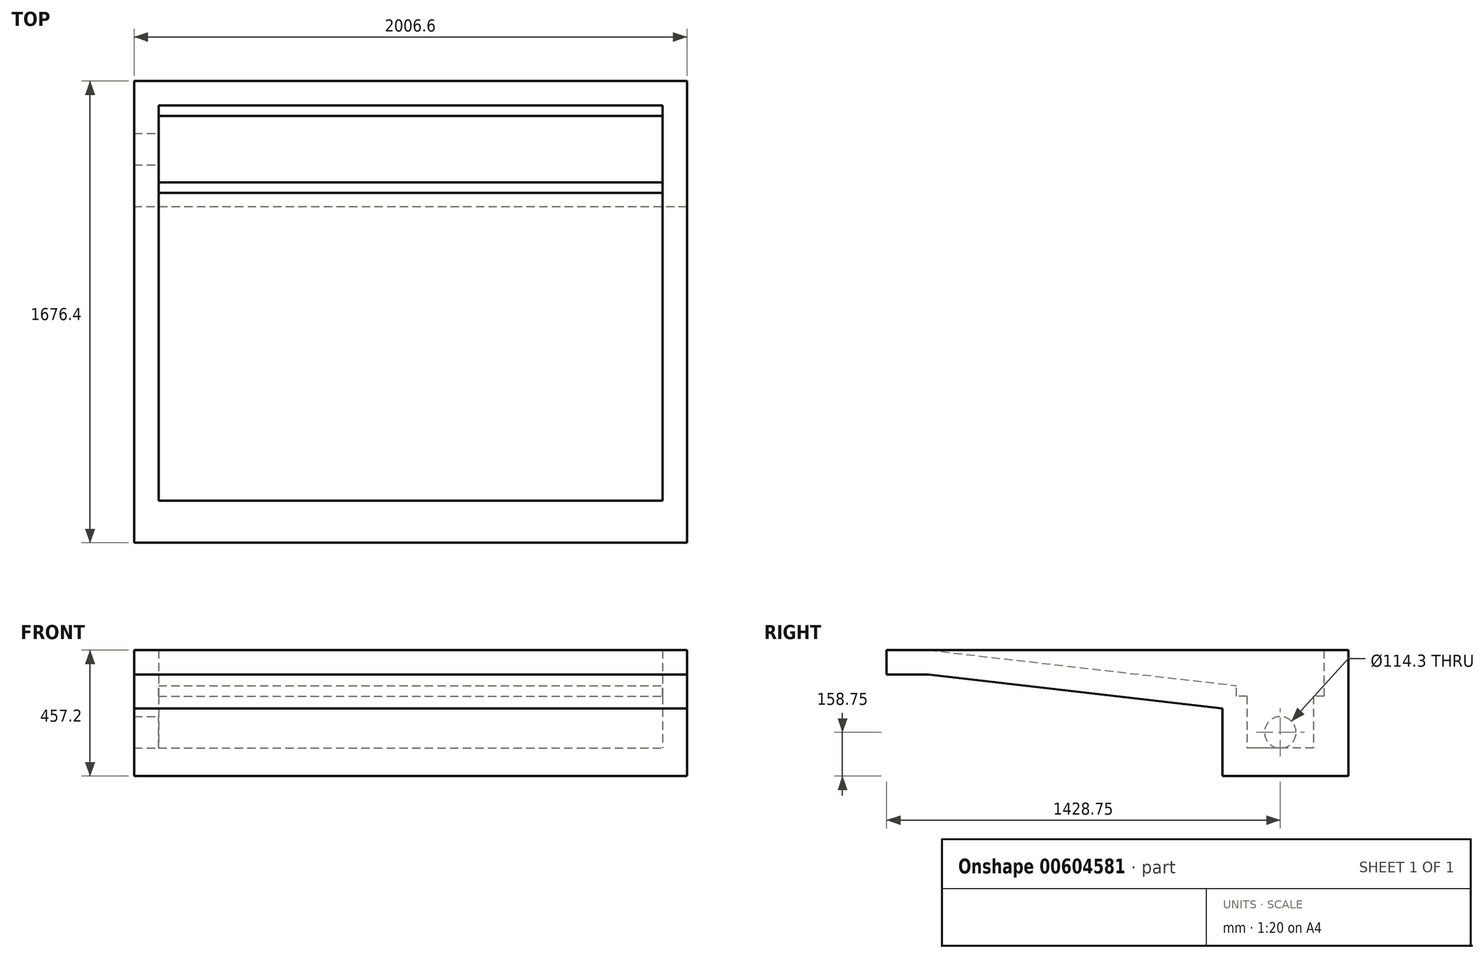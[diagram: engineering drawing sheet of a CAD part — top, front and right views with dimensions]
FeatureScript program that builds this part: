
annotation { "Feature Type Name" : "Feature", "Feature Type Description" : "" }
export const myFeature = defineFeature(function(context is Context, id is Id, definition is map)
    precondition{}
    {
        {
            var Q0;
            Q0=qCreatedBy(makeId("Top.planeOp"),FACE);
            var sketch = newSketch(context, id + "F0", { "sketchPlane" : qUnion([Q0])});
            skLineSegment(sketch, "E0.bottom", {"start": v(1003.3, 762) * mm, "end": v(-1003.3, 762) * mm});
            skLineSegment(sketch, "E0.top", {"start": v(1003.3, -762) * mm, "end": v(-1003.3, -762) * mm});
            skLineSegment(sketch, "E0.left", {"start": v(1003.3, 762) * mm, "end": v(1003.3, -762) * mm});
            skLineSegment(sketch, "E0.right", {"start": v(-1003.3, 762) * mm, "end": v(-1003.3, -762) * mm});
            skPoint(sketch, "E0.middle", {"position": v(0, 0) * mm});
            skSolve(sketch);
        }
        {
            var Q0;
            Q0=qSketchRegion(id+"F0",true);
            extrude(context, id + "F1", {"entities" : qUnion([Q0]), "depth" : 254 * mm, "offsetDistance" : 25.4 * mm});
        }
        {
            var Q0;
            Q0=qCreatedBy(makeId("Right.planeOp"),FACE);
            var sketch = newSketch(context, id + "F2", { "sketchPlane" : qUnion([Q0])});
            skLineSegment(sketch, "E1", {"start": v(-762, 254) * mm, "end": v(673.1, 88.9) * mm});
            skLineSegment(sketch, "E2", {"start": v(673.1, 88.9) * mm, "end": v(673.1, 254) * mm});
            skLineSegment(sketch, "E3", {"start": v(673.1, 254) * mm, "end": v(-762, 254) * mm});
            skLineSegment(sketch, "E4", {"start": v(-762, 165.1) * mm, "end": v(673.1, 0) * mm});
            skLineSegment(sketch, "E5", {"start": v(673.1, 0) * mm, "end": v(-762, 0) * mm});
            skLineSegment(sketch, "E6", {"start": v(-762, 0) * mm, "end": v(-762, 165.1) * mm});
            skSolve(sketch);
        }
        {
            var Q0;
            Q0=makeQuery(id+"F1.opExtrude","SWEPT_FACE",FACE,{"disambiguationData":[OSD([sQuery(id+"F0.wireOp",EDGE,"E0.right")])]});
            var sketch = newSketch(context, id + "F3", { "sketchPlane" : qUnion([Q0])});
            skLineSegment(sketch, "E7.bottom", {"start": v(-762, 254) * mm, "end": v(-304.8, 254) * mm});
            skLineSegment(sketch, "E7.top", {"start": v(-762, -203.2) * mm, "end": v(-304.8, -203.2) * mm});
            skLineSegment(sketch, "E7.left", {"start": v(-762, 254) * mm, "end": v(-762, -203.2) * mm});
            skLineSegment(sketch, "E7.right", {"start": v(-304.8, 254) * mm, "end": v(-304.8, -203.2) * mm});
            skSolve(sketch);
        }
        {
            var Q0;
            Q0=qSketchRegion(id+"F2",true);
            extrude(context, id + "F4", {"entities" : qUnion([Q0]), "operationType" : NewBodyOperationType.REMOVE, "endBound" : BoundingType.SYMMETRIC, "depth" : 1828.8 * mm, "offsetDistance" : 25.4 * mm});
        }
        {
            var Q0;
            Q0=makeQuery(id+"F4.boolean.opBoolean","COPY",FACE,{"derivedFrom":makeQuery(id+"F4.opExtrude","CAP_FACE",FACE,{"disambiguationData":[OSD([sQuery(id+"F2.wireOp",EDGE,"E4"),sQuery(id+"F2.wireOp",EDGE,"E5"),sQuery(id+"F2.wireOp",EDGE,"E6")])],"isStart":true})});
            extrude(context, id + "F5", {"entities" : qUnion([Q0]), "operationType" : NewBodyOperationType.REMOVE, "endBound" : BoundingType.THROUGH_ALL, "oppositeDirection" : true, "depth" : 25.4 * mm, "offsetDistance" : 25.4 * mm});
        }
        {
            var Q0;
            Q0=makeQuery(id+"F4.boolean.opBoolean","COPY",FACE,{"derivedFrom":makeQuery(id+"F4.opExtrude","CAP_FACE",FACE,{"disambiguationData":[OSD([sQuery(id+"F2.wireOp",EDGE,"E4"),sQuery(id+"F2.wireOp",EDGE,"E5"),sQuery(id+"F2.wireOp",EDGE,"E6")])],"isStart":false})});
            extrude(context, id + "F6", {"entities" : qUnion([Q0]), "operationType" : NewBodyOperationType.REMOVE, "endBound" : BoundingType.THROUGH_ALL, "oppositeDirection" : true, "depth" : 25.4 * mm, "offsetDistance" : 25.4 * mm});
        }
        {
            var Q0;
            Q0=qSketchRegion(id+"F3",true);
            var Q1;
            Q1=makeQuery(id+"F1.opExtrude","SWEPT_FACE",FACE,{"disambiguationData":[OSD([sQuery(id+"F0.wireOp",EDGE,"E0.left")])]});
            extrude(context, id + "F7", {"entities" : qUnion([Q0]), "operationType" : NewBodyOperationType.ADD, "endBound" : BoundingType.UP_TO_SURFACE, "oppositeDirection" : true, "depth" : 25.4 * mm, "endBoundEntityFace" : qUnion([Q1]), "offsetDistance" : 25.4 * mm});
        }
        {
            var Q0;
            Q0=makeQuery(id+"F2.imprint","IMPRINT",FACE,{"disambiguationData":[TD([[makeQuery(id+"F2.imprint","IMPRINT",EDGE,{"derivedFrom":sQuery(id+"F2.wireOp",EDGE,"E1")}),1.0]])]});
            var Q1;
            Q1=makeQuery(id+"F4.boolean.opBoolean","COPY",FACE,{"derivedFrom":makeQuery(id+"F4.opExtrude","CAP_FACE",FACE,{"disambiguationData":[OSD([sQuery(id+"F2.wireOp",EDGE,"E1"),sQuery(id+"F2.wireOp",EDGE,"E2"),sQuery(id+"F2.wireOp",EDGE,"E3")])],"isStart":true})});
            var Q2;
            Q2=makeQuery(id+"F4.boolean.opBoolean","COPY",FACE,{"derivedFrom":makeQuery(id+"F4.opExtrude","CAP_FACE",FACE,{"disambiguationData":[OSD([sQuery(id+"F2.wireOp",EDGE,"E1"),sQuery(id+"F2.wireOp",EDGE,"E2"),sQuery(id+"F2.wireOp",EDGE,"E3")])],"isStart":false})});
            extrude(context, id + "F8", {"entities" : qUnion([Q0]), "operationType" : NewBodyOperationType.REMOVE, "endBound" : BoundingType.UP_TO_SURFACE, "oppositeDirection" : true, "depth" : 25.4 * mm, "endBoundEntityFace" : qUnion([Q1]), "offsetDistance" : 25.4 * mm, "hasSecondDirection" : true, "secondDirectionBound" : SecondDirectionBoundingType.UP_TO_SURFACE, "secondDirectionOppositeDirection" : false, "secondDirectionDepth" : 25.4 * mm, "secondDirectionBoundEntityFace" : qUnion([Q2])});
        }
        {
            var Q0;
            Q0=makeQuery(id+"F7.boolean.opBoolean","MERGE",FACE,{"derivedFrom":[makeQuery(id+"F1.opExtrude","CAP_FACE",FACE,{"disambiguationData":[OSD([sQuery(id+"F0.wireOp",EDGE,"E0.bottom"),sQuery(id+"F0.wireOp",EDGE,"E0.top"),sQuery(id+"F0.wireOp",EDGE,"E0.left"),sQuery(id+"F0.wireOp",EDGE,"E0.right")])],"isStart":false}),makeQuery(id+"F7.opExtrude","SWEPT_FACE",FACE,{"disambiguationData":[OSD([sQuery(id+"F3.wireOp",EDGE,"E7.bottom")])]})]});
            var sketch = newSketch(context, id + "F9", { "sketchPlane" : qUnion([Q0])});
            skLineSegment(sketch, "E8.bottom", {"start": v(-914.4, 673.1) * mm, "end": v(914.4, 673.1) * mm});
            skLineSegment(sketch, "E8.top", {"start": v(-914.4, 355.6) * mm, "end": v(914.4, 355.6) * mm});
            skLineSegment(sketch, "E8.left", {"start": v(-914.4, 673.1) * mm, "end": v(-914.4, 355.6) * mm});
            skLineSegment(sketch, "E8.right", {"start": v(914.4, 673.1) * mm, "end": v(914.4, 355.6) * mm});
            skSolve(sketch);
        }
        {
            var Q0;
            Q0=qSketchRegion(id+"F9",true);
            var Q1;
            Q1=makeQuery(id+"F7.opExtrude","SWEPT_FACE",FACE,{"disambiguationData":[OSD([sQuery(id+"F3.wireOp",EDGE,"E7.top")])]});
            extrude(context, id + "F10", {"entities" : qUnion([Q0]), "operationType" : NewBodyOperationType.REMOVE, "endBound" : BoundingType.UP_TO_SURFACE, "oppositeDirection" : true, "depth" : 25.4 * mm, "endBoundEntityFace" : qUnion([Q1]), "hasOffset" : true, "offsetDistance" : 101.6 * mm});
        }
        {
            var Q0;
            Q0=makeQuery(id+"F10.boolean.opBoolean","COPY",FACE,{"derivedFrom":makeQuery(id+"F10.opExtrude","CAP_FACE",FACE,{"disambiguationData":[OSD([sQuery(id+"F9.wireOp",EDGE,"E8.bottom"),sQuery(id+"F9.wireOp",EDGE,"E8.top"),sQuery(id+"F9.wireOp",EDGE,"E8.left"),sQuery(id+"F9.wireOp",EDGE,"E8.right")])],"isStart":false})});
            var sketch = newSketch(context, id + "F11", { "sketchPlane" : qUnion([Q0])});
            skLineSegment(sketch, "E9.bottom", {"start": v(914.4, 673.1) * mm, "end": v(-914.4, 673.1) * mm});
            skLineSegment(sketch, "E9.top", {"start": v(914.4, 635) * mm, "end": v(-914.4, 635) * mm});
            skLineSegment(sketch, "E9.left", {"start": v(914.4, 673.1) * mm, "end": v(914.4, 635) * mm});
            skLineSegment(sketch, "E9.right", {"start": v(-914.4, 673.1) * mm, "end": v(-914.4, 635) * mm});
            skLineSegment(sketch, "E10.bottom", {"start": v(-914.4, 355.6) * mm, "end": v(914.4, 355.6) * mm});
            skLineSegment(sketch, "E10.top", {"start": v(-914.4, 393.7) * mm, "end": v(914.4, 393.7) * mm});
            skLineSegment(sketch, "E10.left", {"start": v(-914.4, 355.6) * mm, "end": v(-914.4, 393.7) * mm});
            skLineSegment(sketch, "E10.right", {"start": v(914.4, 355.6) * mm, "end": v(914.4, 393.7) * mm});
            skSolve(sketch);
        }
        {
            var Q0;
            Q0=qSketchRegion(id+"F11",true);
            var Q1;
            {var subQ0=sQuery(id+"F2.wireOp",EDGE,"E1");Q1=makeQuery(id+"F10.boolean.opBoolean","INTERSECT",VERTEX,{"disambiguationData":[OD(1.0)],"derivedFrom":[makeQuery(id+"F8.boolean.opBoolean","MERGE",FACE,{"derivedFrom":[makeQuery(id+"F4.boolean.opBoolean","COPY",FACE,{"derivedFrom":makeQuery(id+"F4.opExtrude","SWEPT_FACE",FACE,{"disambiguationData":[OSD([subQ0])]})})],"fromTools":[makeQuery(id+"F8.opExtrude","SWEPT_FACE",FACE,{"disambiguationData":[OSD([subQ0])]})]}),makeQuery(id+"F10.opExtrude","SWEPT_FACE",FACE,{"disambiguationData":[OSD([sQuery(id+"F9.wireOp",EDGE,"E8.top")])]})]});}
            extrude(context, id + "F12", {"entities" : qUnion([Q0]), "operationType" : NewBodyOperationType.ADD, "endBound" : BoundingType.UP_TO_VERTEX, "depth" : 25.4 * mm, "endBoundEntityVertex" : qUnion([Q1]), "hasOffset" : true, "offsetDistance" : 38.1 * mm});
        }
        {
            var Q0;
            {var subQ0=sQuery(id+"F2.wireOp",EDGE,"E3");var subQ1=sQuery(id+"F2.wireOp",EDGE,"E2");var subQ2=sQuery(id+"F2.wireOp",EDGE,"E1");Q0=makeQuery(id+"F10.boolean.opBoolean","MERGE",FACE,{"derivedFrom":[makeQuery(id+"F8.boolean.opBoolean","MERGE",FACE,{"derivedFrom":[makeQuery(id+"F4.boolean.opBoolean","COPY",FACE,{"derivedFrom":makeQuery(id+"F4.opExtrude","CAP_FACE",FACE,{"disambiguationData":[OSD([subQ2,subQ1,subQ0])],"isStart":true})})],"fromTools":[makeQuery(id+"F8.opExtrude","CAP_FACE",FACE,{"disambiguationData":[OSD([subQ2,subQ1,subQ0])],"isStart":false})]})],"fromTools":[makeQuery(id+"F10.opExtrude","SWEPT_FACE",FACE,{"disambiguationData":[OSD([sQuery(id+"F9.wireOp",EDGE,"E8.left")])]})]});}
            var sketch = newSketch(context, id + "F13", { "sketchPlane" : qUnion([Q0])});
            skCircle(sketch, "E11", {"center": v(514.35, -44.45) * mm, "radius": 57.15 * mm});
            skLineSegment(sketch, "E12", {"start": v(514.35, -44.45) * mm, "end": v(514.35, -101.6) * mm, "construction": true});
            skSolve(sketch);
        }
        {
            var Q0;
            Q0=qSketchRegion(id+"F13",true);
            extrude(context, id + "F14", {"entities" : qUnion([Q0]), "operationType" : NewBodyOperationType.REMOVE, "endBound" : BoundingType.THROUGH_ALL, "oppositeDirection" : true, "depth" : 25.4 * mm, "offsetDistance" : 25.4 * mm});
        }
        {
            var Q0;
            Q0=makeQuery(id+"F1.opExtrude","SWEPT_FACE",FACE,{"disambiguationData":[OSD([sQuery(id+"F0.wireOp",EDGE,"E0.top")])]});
            extrude(context, id + "F15", {"entities" : qUnion([Q0]), "operationType" : NewBodyOperationType.ADD, "depth" : 152.4 * mm, "offsetDistance" : 25.4 * mm});
        }
    });
